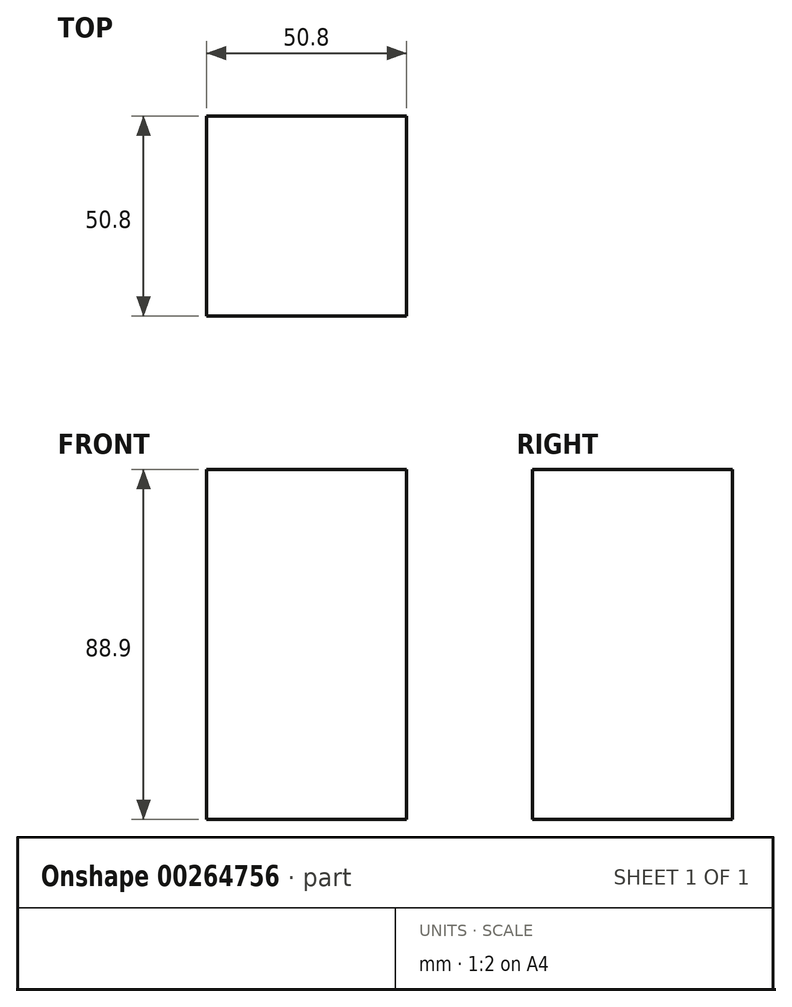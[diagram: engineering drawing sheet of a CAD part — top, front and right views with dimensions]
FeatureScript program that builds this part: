
annotation { "Feature Type Name" : "Feature", "Feature Type Description" : "" }
export const myFeature = defineFeature(function(context is Context, id is Id, definition is map)
    precondition{}
    {
        {
            var Q0;
            Q0=qCreatedBy(makeId("Top.planeOp"),FACE);
            var sketch = newSketch(context, id + "F0", { "sketchPlane" : qUnion([Q0])});
            skLineSegment(sketch, "E0.bottom", {"start": v(-25.4, 26.2) * mm, "end": v(25.4, 26.2) * mm});
            skLineSegment(sketch, "E0.top", {"start": v(-25.4, -24.6) * mm, "end": v(25.4, -24.6) * mm});
            skLineSegment(sketch, "E0.left", {"start": v(-25.4, 26.2) * mm, "end": v(-25.4, -24.6) * mm});
            skLineSegment(sketch, "E0.right", {"start": v(25.4, 26.2) * mm, "end": v(25.4, -24.6) * mm});
            skSolve(sketch);
        }
        {
            var Q0;
            Q0 = qSketchRegion(id + "F0", true);
            extrude(context, id + "F1", {"entities" : qUnion([Q0]), "depth" : 88.9 * mm});
        }
    });
